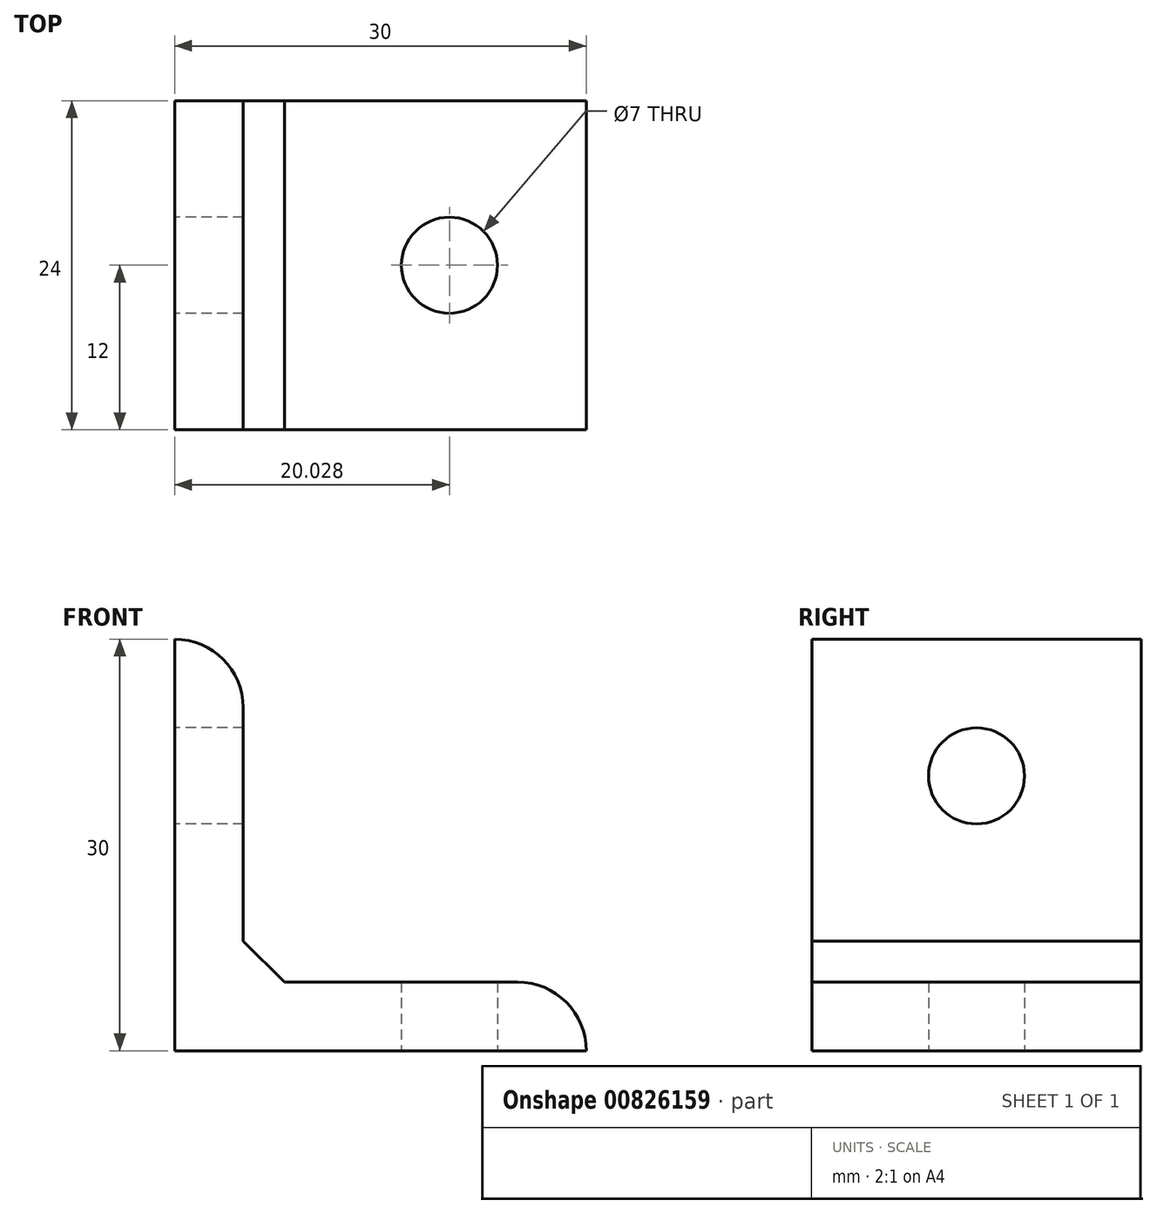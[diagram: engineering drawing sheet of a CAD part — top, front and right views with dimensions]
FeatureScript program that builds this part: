
annotation { "Feature Type Name" : "Feature", "Feature Type Description" : "" }
export const myFeature = defineFeature(function(context is Context, id is Id, definition is map)
    precondition{}
    {
        {
            var Q0;
            Q0=qCreatedBy(makeId("Front.planeOp"),FACE);
            var sketch = newSketch(context, id + "F0", { "sketchPlane" : qUnion([Q0])});
            skLineSegment(sketch, "E0", {"start": v(0, 30) * mm, "end": v(0, 0) * mm});
            skLineSegment(sketch, "E1", {"start": v(0, 0) * mm, "end": v(30, 0) * mm});
            skArc(sketch, "E2", {"start": v(5, 25) * mm, "mid": v(3.54, 28.54) * mm, "end": v(0, 30) * mm});
            skLineSegment(sketch, "E3", {"start": v(5, 25) * mm, "end": v(5, 8) * mm});
            skLineSegment(sketch, "E4", {"start": v(8, 5) * mm, "end": v(5, 8) * mm});
            skLineSegment(sketch, "E5", {"start": v(-0.55, 20) * mm, "end": v(5.57, 20) * mm});
            skLineSegment(sketch, "E6", {"start": v(20, -0.55) * mm, "end": v(20, 5.57) * mm});
            skLineSegment(sketch, "E7", {"start": v(25, 5) * mm, "end": v(8, 5) * mm});
            skArc(sketch, "E8", {"start": v(30, 0) * mm, "mid": v(28.54, 3.54) * mm, "end": v(25, 5) * mm});
            skSolve(sketch);
        }
        {
            var Q0;
            {var subQ0=sQuery(id+"F0.wireOp",EDGE,"E2");Q0=makeQuery(id+"F0.imprint","IMPRINT",FACE,{"disambiguationData":[TD([[makeQuery(id+"F0.imprint","IMPRINT",EDGE,{"derivedFrom":subQ0}),1.0]])]});}
            var Q1;
            {var subQ0=sQuery(id+"F0.wireOp",EDGE,"E8");Q1=makeQuery(id+"F0.imprint","IMPRINT",FACE,{"disambiguationData":[TD([[makeQuery(id+"F0.imprint","IMPRINT",EDGE,{"derivedFrom":subQ0}),1.0]])]});}
            var Q2;
            {var subQ0=sQuery(id+"F0.wireOp",EDGE,"E4");Q2=makeQuery(id+"F0.imprint","IMPRINT",FACE,{"disambiguationData":[TD([[makeQuery(id+"F0.imprint","IMPRINT",EDGE,{"derivedFrom":subQ0}),1.0]])]});}
            extrude(context, id + "F1", {"entities" : qUnion([Q0, Q1, Q2]), "oppositeDirection" : true, "depth" : 24 * mm, "offsetDistance" : 25 * mm});
        }
        {
            var Q0;
            Q0=qCreatedBy(makeId("Right.planeOp"),FACE);
            var sketch = newSketch(context, id + "F2", { "sketchPlane" : qUnion([Q0])});
            skLineSegment(sketch, "E9", {"start": v(0, 30.03) * mm, "end": v(0, 3.87) * mm});
            skPoint(sketch, "E10", {"position": v(12, 20.03) * mm});
            skCircle(sketch, "E11", {"center": v(12, 20.03) * mm, "radius": 3.5 * mm});
            skSolve(sketch);
        }
        {
            var Q0;
            Q0 = qSketchRegion(id + "F2", true);
            extrude(context, id + "F3", {"entities" : qUnion([Q0]), "operationType" : NewBodyOperationType.REMOVE, "depth" : 6 * mm, "offsetDistance" : 25 * mm});
        }
        {
            var Q0;
            Q0=makeQuery(id+"F1.opExtrude","SWEPT_FACE",FACE,{"disambiguationData":[OSD([sQuery(id+"F0.wireOp",EDGE,"E1")])]});
            var sketch = newSketch(context, id + "F4", { "sketchPlane" : qUnion([Q0])});
            skCircle(sketch, "E12", {"center": v(20.03, -12) * mm, "radius": 3.5 * mm});
            skSolve(sketch);
        }
        {
            var Q0;
            Q0=makeQuery(id+"F4.imprint","IMPRINT",FACE,{"disambiguationData":[TD([[makeQuery(id+"F4.imprint","IMPRINT",EDGE,{"derivedFrom":sQuery(id+"F4.wireOp",EDGE,"E12")}),1.0]])]});
            extrude(context, id + "F5", {"entities" : qUnion([Q0]), "operationType" : NewBodyOperationType.REMOVE, "oppositeDirection" : true, "depth" : 6 * mm, "offsetDistance" : 25 * mm});
        }
    });
